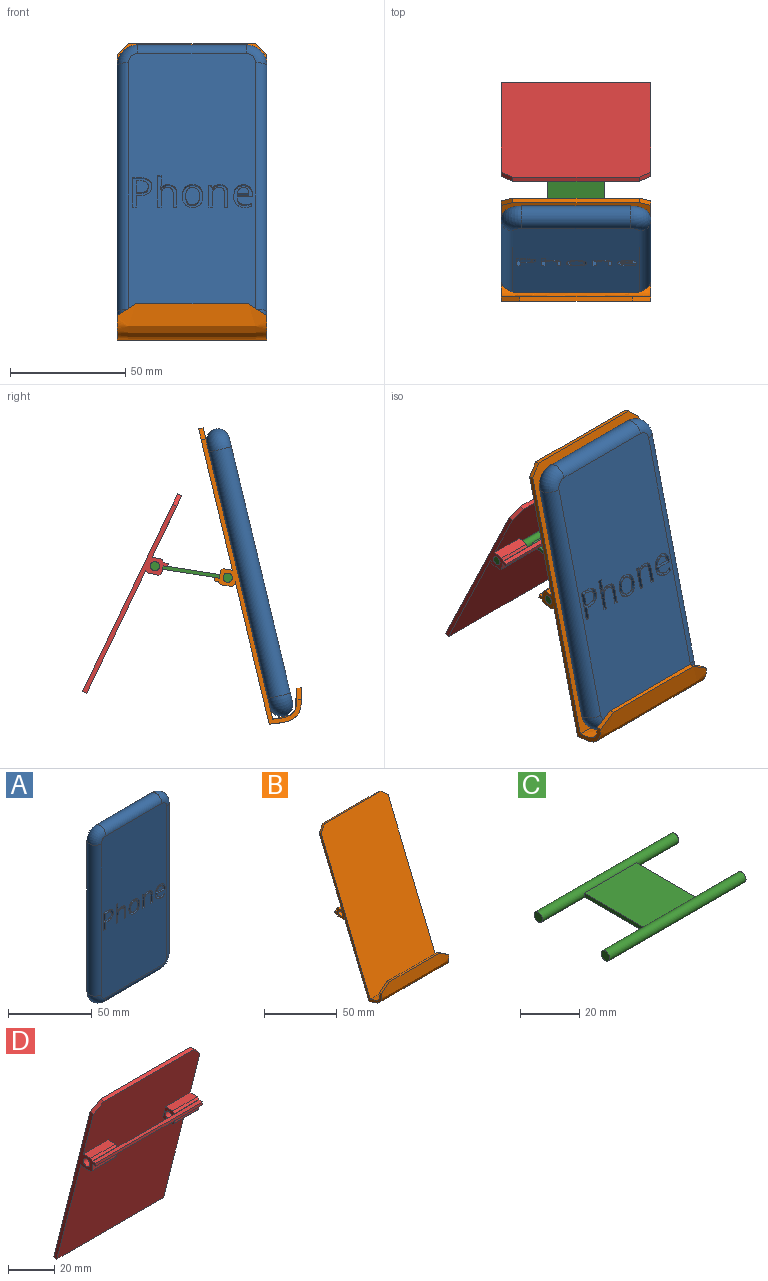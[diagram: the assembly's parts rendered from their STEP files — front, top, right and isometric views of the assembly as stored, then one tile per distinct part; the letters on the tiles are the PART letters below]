
ASSEMBLY  parts=4 mates=3
PART A: 104 faces, bbox 65x10x128 mm
  f0: plane 118x55mm, normal (0,-1,0), area 6209.6mm2, adj f2,f3,f4,f5,f6,f7,f8,f9
  f1: plane 118x55mm, normal (0,1,0), area 6476.3mm2, adj f2,f3,f4,f5,f6,f7,f8,f9
  f2: cylinder r=5mm len=110mm, axis (0,0,1), area 1727.9mm2, adj f0,f1,f3,f4
  f3: torus R=4mm, axis (0,-1,0), area 177.2mm2, adj f0,f1,f2,f5
  f4: torus R=4mm, axis (0,-1,0), area 177.2mm2, adj f0,f1,f2,f6
  f5: cylinder r=5mm len=47mm, axis (-1,0,0), area 738.3mm2, adj f0,f1,f3,f7
  f6: cylinder r=5mm len=47mm, axis (1,0,0), area 738.3mm2, adj f0,f1,f4,f8
  f7: torus R=4mm, axis (0,-1,0), area 177.2mm2, adj f0,f1,f5,f9
  f8: torus R=4mm, axis (0,-1,0), area 177.2mm2, adj f0,f1,f6,f9
  f9: cylinder r=5mm len=110mm, axis (0,0,-1), area 1727.9mm2, adj f0,f1,f7,f8
  f10: plane 6.33x2mm, normal (1,0,0), area 12.7mm2, adj f0,f11,f27,f28
  f11: plane 2x1.48mm, normal (0,0,1), area 3mm2, adj f0,f10,f12,f28
  f12: plane 6.38x2mm, normal (-1,0,0), area 12.8mm2, adj f0,f11,f13,f28
  f13: extruded ~2.71x2mm, area 5.9mm2, adj f0,f12,f14,f28
  f14: extruded ~2.69x2mm, area 5.8mm2, adj f0,f13,f15,f28
  f15: extruded ~2x1.84mm, area 3.8mm2, adj f0,f14,f16,f28
  f16: extruded ~2x1.25mm, area 3.4mm2, adj f0,f15,f17,f28
  f17: plane 2x0.09mm, normal (0,0,-1), area 0.2mm2, adj f0,f16,f18,f28
  f18: extruded ~2x1.26mm, area 2.5mm2, adj f0,f17,f19,f28
  f19: plane 4.21x2mm, normal (-1,0,0), area 8.4mm2, adj f0,f18,f20,f28
  f20: plane 2x1.48mm, normal (0,0,-1), area 3mm2, adj f0,f19,f21,f28
  f21: plane 13.9x2mm, normal (1,0,0), area 27.8mm2, adj f0,f20,f22,f28
  f22: plane 2x1.48mm, normal (0,0,1), area 3mm2, adj f0,f21,f23,f28
  f23: plane 5.12x2mm, normal (-1,0,0), area 10.2mm2, adj f0,f22,f24,f28
  f24: extruded ~2.75x2mm, area 5.8mm2, adj f0,f23,f25,f28
  f25: extruded ~2.25x2mm, area 5mm2, adj f0,f24,f26,f28
  f26: extruded ~2x1.71mm, area 3.7mm2, adj f0,f25,f27,f28
  f27: extruded ~2x1.78mm, area 3.8mm2, adj f0,f10,f26,f28
  f28: plane 13.9x8.18mm, normal (0,-1,0), area 40.9mm2, adj f10,f11,f12,f13,f14,f15,f16,f17
  f29: extruded ~2x1.88mm, area 4.2mm2, adj f30,f47,f48,f101
  f30: extruded ~2x1.79mm, area 4mm2, adj f29,f31,f48,f101
  f31: extruded ~2.15x2mm, area 4.6mm2, adj f30,f32,f48,f101
  f32: plane 5.12x2mm, normal (0,0,-1), area 10.2mm2, adj f31,f47,f48,f101
  f33: extruded ~3.43x2mm, area 7.6mm2, adj f0,f34,f46,f48
  f34: extruded ~2x1.69mm, area 3.4mm2, adj f0,f33,f35,f48
  f35: extruded ~2x1.49mm, area 3.1mm2, adj f0,f34,f36,f48
  f36: plane 2x1.32mm, normal (-1,0,0), area 2.6mm2, adj f0,f35,f37,f48
  f37: extruded ~3.12x2mm, area 6.4mm2, adj f0,f36,f38,f48
  f38: extruded ~2.33x2mm, area 5.1mm2, adj f0,f37,f39,f48
  f39: extruded ~2.62x2mm, area 5.6mm2, adj f0,f38,f40,f48
  f40: plane 6.74x2mm, normal (0,0,1), area 13.5mm2, adj f0,f39,f41,f48
  f41: plane 2x0.94mm, normal (-1,0,0), area 1.9mm2, adj f0,f40,f42,f48
  f42: extruded ~3.19x2mm, area 6.9mm2, adj f0,f41,f43,f48
  f43: extruded ~2.91x2mm, area 6.5mm2, adj f0,f42,f44,f48
  f44: extruded ~3.13x2mm, area 7.1mm2, adj f0,f43,f45,f48
  f45: extruded ~3.76x2mm, area 8mm2, adj f0,f44,f46,f48
  f46: extruded ~3.67x2mm, area 8mm2, adj f0,f33,f45,f48
  f47: extruded ~2.12x2mm, area 4.6mm2, adj f29,f32,f48,f101
  f48: plane 10.15x8.28mm, normal (0,-1,0), area 38.2mm2, adj f29,f30,f31,f32,f33,f34,f35,f36
  f49: extruded ~2.86x2mm, area 6mm2, adj f50,f65,f66,f102
  f50: extruded ~2.85x2mm, area 6mm2, adj f49,f51,f66,f102
  f51: extruded ~2.2x2mm, area 5mm2, adj f50,f52,f66,f102
  f52: extruded ~2.23x2mm, area 5mm2, adj f51,f53,f66,f102
  f53: extruded ~2.84x2mm, area 6mm2, adj f52,f54,f66,f102
  f54: extruded ~2.86x2mm, area 6mm2, adj f53,f55,f66,f102
  f55: extruded ~2.21x2mm, area 5mm2, adj f54,f65,f66,f102
  f56: extruded ~3.74x2mm, area 8mm2, adj f0,f57,f64,f66
  f57: extruded ~3.7x2mm, area 8mm2, adj f0,f56,f58,f66
  f58: extruded ~3.26x2mm, area 7.3mm2, adj f0,f57,f59,f66
  f59: extruded ~3.32x2mm, area 7.4mm2, adj f0,f58,f60,f66
  f60: extruded ~3.73x2mm, area 8mm2, adj f0,f59,f61,f66
  f61: extruded ~2.7x2mm, area 5.6mm2, adj f0,f60,f62,f66
  f62: extruded ~2x1.77mm, area 4.8mm2, adj f0,f61,f63,f66
  f63: extruded ~2.33x2mm, area 4.9mm2, adj f0,f62,f64,f66
  f64: extruded ~3.33x2mm, area 7.4mm2, adj f0,f56,f63,f66
  f65: extruded ~2.2x2mm, area 5mm2, adj f49,f55,f66,f102
  f66: plane 10.15x8.99mm, normal (0,-1,0), area 36.8mm2, adj f49,f50,f51,f52,f53,f54,f55,f56
  f67: plane 2x1.37mm, normal (0,0,-1), area 2.7mm2, adj f68,f81,f82,f103
  f68: plane 5.3x2mm, normal (-1,0,0), area 10.6mm2, adj f67,f69,f82,f103
  f69: plane 2x1.7mm, normal (0,0,1), area 3.4mm2, adj f68,f70,f82,f103
  f70: extruded ~2.64x2mm, area 5.5mm2, adj f69,f71,f82,f103
  f71: extruded ~2x1.93mm, area 4.4mm2, adj f70,f72,f82,f103
  f72: extruded ~2.09x2mm, area 4.7mm2, adj f71,f81,f82,f103
  f73: extruded ~3.05x2mm, area 6.9mm2, adj f0,f74,f80,f82
  f74: extruded ~4.89x3.8mm, area 14.2mm2, adj f0,f73,f75,f82
  f75: plane 3.39x2mm, normal (0,0,-1), area 6.8mm2, adj f0,f74,f76,f82
  f76: plane 13.06x2mm, normal (1,0,0), area 26.1mm2, adj f0,f75,f77,f82
  f77: plane 2x1.52mm, normal (0,0,1), area 3mm2, adj f0,f76,f78,f82
  f78: plane 5.14x2mm, normal (-1,0,0), area 10.3mm2, adj f0,f77,f79,f82
  f79: plane 2x1.54mm, normal (0,0,1), area 3.1mm2, adj f0,f78,f80,f82
  f80: extruded ~3.87x2mm, area 8.2mm2, adj f0,f73,f79,f82
  f81: extruded ~2.92x2mm, area 6.1mm2, adj f67,f72,f82,f103
  f82: plane 13.06x8.28mm, normal (0,-1,0), area 42mm2, adj f67,f68,f69,f70,f71,f72,f73,f74
  f83: plane 6.33x2mm, normal (1,0,0), area 12.7mm2, adj f0,f84,f99,f100
  f84: plane 2x1.48mm, normal (0,0,1), area 3mm2, adj f0,f83,f85,f100
  f85: plane 6.38x2mm, normal (-1,0,0), area 12.8mm2, adj f0,f84,f86,f100
  f86: extruded ~2.73x2mm, area 5.9mm2, adj f0,f85,f87,f100
  f87: extruded ~2.66x2mm, area 5.7mm2, adj f0,f86,f88,f100
  f88: extruded ~2x1.83mm, area 3.8mm2, adj f0,f87,f89,f100
  f89: extruded ~2x1.28mm, area 3.4mm2, adj f0,f88,f90,f100
  f90: plane 2x0.07mm, normal (0,0,-1), area 0.1mm2, adj f0,f89,f91,f100
  f91: plane 2x1.34mm, normal (-0.98,0,-0.18), area 2.7mm2, adj f0,f90,f92,f100
  f92: plane 2x1.21mm, normal (0,0,-1), area 2.4mm2, adj f0,f91,f93,f100
  f93: plane 9.79x2mm, normal (1,0,0), area 19.6mm2, adj f0,f92,f94,f100
  f94: plane 2x1.48mm, normal (0,0,1), area 3mm2, adj f0,f93,f95,f100
  f95: plane 5.14x2mm, normal (-1,0,0), area 10.3mm2, adj f0,f94,f96,f100
  f96: extruded ~2.74x2mm, area 5.8mm2, adj f0,f95,f97,f100
  f97: extruded ~2.25x2mm, area 5mm2, adj f0,f96,f98,f100
  f98: extruded ~2x1.71mm, area 3.7mm2, adj f0,f97,f99,f100
  f99: extruded ~2x1.78mm, area 3.8mm2, adj f0,f83,f98,f100
  f100: plane 9.97x8.18mm, normal (0,-1,0), area 34.7mm2, adj f83,f84,f85,f86,f87,f88,f89,f90
  f101: plane 5.12x2.89mm, normal (0,-1,0), area 11.9mm2, adj f29,f30,f31,f32,f47
  f102: plane 7.64x5.92mm, normal (0,-1,0), area 37.6mm2, adj f49,f50,f51,f52,f53,f54,f55,f65
  f103: plane 5.3x5.19mm, normal (0,-1,0), area 24.5mm2, adj f67,f68,f69,f70,f71,f72,f81
PART B: 36 faces, bbox 65x62.6x122.6 mm
  f0: plane 15x3.3mm, normal (0,1,0), area 49.5mm2, adj f6,f15,f27,f33
  f1: plane 15x0.2mm, normal (0,1,0), area 3mm2, adj f4,f21,f24,f34
  f2: plane 121.78x65mm, normal (0,0.92,-0.38), area 8383.6mm2, adj f3,f4,f6,f9,f10,f14,f15,f16
  f3: plane 55x1.85mm, normal (0,0.38,0.92), area 110mm2, adj f2,f8,f28,f29
  f4: plane 117.92x60.71mm, normal (-1,0,0), area 320.8mm2, adj f1,f2,f7,f8,f9,f16,f17,f18
  f5: plane 49x1.96mm, normal (0,0.21,0.98), area 98mm2, adj f7,f9,f30,f31
  f6: plane 117.92x60.71mm, normal (1,0,0), area 320.8mm2, adj f0,f2,f7,f8,f9,f10,f11,f12
  f7: extruded ~65x14.92mm, area 1294.1mm2, adj f4,f5,f6,f8,f30,f31
  f8: plane 120.17x65mm, normal (0,-0.92,0.38), area 8425mm2, adj f3,f4,f6,f7,f28,f29
  f9: extruded ~65x17.71mm, area 1605.3mm2, adj f2,f4,f5,f6,f30,f31
  f10: plane 15x1.22mm, normal (0,-1,0), area 18.3mm2, adj f2,f6,f15,f23
  f11: plane 15x5mm, normal (0,0,-1), area 75mm2, adj f6,f15,f23,f26
  f12: plane 15x0.2mm, normal (0,1,0), area 3mm2, adj f6,f15,f26,f34
  f13: cylinder r=2mm len=15mm, axis (1,0,0), area 188.5mm2, adj f6,f15
  f14: plane 15x4.03mm, normal (0,0,1), area 60.4mm2, adj f2,f6,f15,f27
  f15: plane 7x7mm, normal (-1,0,0), area 30.2mm2, adj f0,f2,f10,f11,f12,f13,f14,f23
  f16: plane 15x4.03mm, normal (0,0,1), area 60.4mm2, adj f2,f4,f21,f25
  f17: plane 15x3.3mm, normal (0,1,0), area 49.5mm2, adj f4,f21,f25,f33
  f18: plane 15x5mm, normal (0,0,-1), area 75mm2, adj f4,f21,f22,f24
  f19: cylinder r=2mm len=15mm, axis (-1,0,0), area 188.5mm2, adj f4,f21
  f20: plane 15x1.22mm, normal (0,-1,0), area 18.3mm2, adj f2,f4,f21,f22
  f21: plane 7x7mm, normal (1,0,0), area 30.2mm2, adj f1,f2,f16,f17,f18,f19,f20,f22
  f22: plane 15x1mm, normal (0,-0.71,-0.71), area 21.2mm2, adj f4,f18,f20,f21
  f23: plane 15x1mm, normal (0,-0.71,-0.71), area 21.2mm2, adj f6,f10,f11,f15
  f24: plane 15x1mm, normal (0,0.71,-0.71), area 21.2mm2, adj f1,f4,f18,f21
  f25: plane 15x1mm, normal (0,0.71,0.71), area 21.2mm2, adj f4,f16,f17,f21
  f26: plane 15x1mm, normal (0,0.71,-0.71), area 21.2mm2, adj f6,f11,f12,f15
  f27: plane 15x1mm, normal (0,0.71,0.71), area 21.2mm2, adj f0,f6,f14,f15
  f28: plane 5.39x5mm, normal (-0.71,0.27,0.65), area 14.1mm2, adj f2,f3,f4,f8
  f29: plane 5.39x5mm, normal (0.71,0.27,0.65), area 14.1mm2, adj f2,f3,f6,f8
  f30: plane 8.02x5.35mm, normal (-0.53,0.17,0.83), area 18.9mm2, adj f4,f5,f7,f9
  f31: plane 8.02x5.35mm, normal (0.53,0.17,0.83), area 18.9mm2, adj f5,f6,f7,f9
  f32: plane 35x1.5mm, normal (0,-1,0), area 52.5mm2, adj f15,f21,f33,f34
  f33: plane 65x2mm, normal (0,0,1), area 130mm2, adj f0,f4,f6,f17,f32,f35
  f34: plane 65x2mm, normal (0,0,-1), area 130mm2, adj f1,f4,f6,f12,f32,f35
  f35: plane 65x1.5mm, normal (0,1,0), area 97.5mm2, adj f4,f6,f33,f34
PART C: 10 faces, bbox 65x36x4 mm
  f0: plane 28.33x1.6mm, normal (1,0,0), area 45mm2, adj f1,f3,f4,f7
  f1: plane 28.33x25mm, normal (0,0,-1), area 708.3mm2, adj f0,f2,f4,f7
  f2: plane 28.33x1.6mm, normal (-1,0,0), area 45mm2, adj f1,f3,f4,f7
  f3: plane 28.33x25mm, normal (0,0,1), area 708.3mm2, adj f0,f2,f4,f7
  f4: cylinder r=2mm len=65mm, axis (1,0,0), area 775.7mm2, adj f0,f1,f2,f3,f5,f6
  f5: plane 4x4mm, normal (1,0,0), area 12.6mm2, adj f4
  f6: plane 4x4mm, normal (-1,0,0), area 12.6mm2, adj f4
  f7: cylinder r=2mm len=65mm, axis (1,0,0), area 775.7mm2, adj f0,f1,f2,f3,f8,f9
  f8: plane 4x4mm, normal (1,0,0), area 12.6mm2, adj f7
  f9: plane 4x4mm, normal (-1,0,0), area 12.6mm2, adj f7
PART D: 30 faces, bbox 65x25.5x92.7 mm
  f0: plane 15x0.2mm, normal (0,-1,0), area 3mm2, adj f3,f8,f10,f27
  f1: plane 15x0.2mm, normal (0,-1,0), area 3mm2, adj f12,f17,f23,f27
  f2: plane 15x4.45mm, normal (0,0,1), area 66.7mm2, adj f3,f8,f10,f11
  f3: plane 7x6.98mm, normal (-1,0,0), area 30.2mm2, adj f0,f2,f4,f5,f6,f7,f9,f10
  f4: plane 15x0.98mm, normal (0,0.71,-0.71), area 20.8mm2, adj f3,f6,f8,f11
  f5: plane 15x3.3mm, normal (0,-1,0), area 49.5mm2, adj f3,f8,f9,f29
  f6: plane 15x5mm, normal (0,0,-1), area 75mm2, adj f3,f4,f8,f9
  f7: cylinder r=2mm len=15mm, axis (1,0,0), area 188.5mm2, adj f3,f8
  f8: plane 87.89x25.52mm, normal (1,0,0), area 213.6mm2, adj f0,f2,f4,f5,f6,f7,f9,f10
  f9: plane 15x1mm, normal (0,-0.71,-0.71), area 21.2mm2, adj f3,f5,f6,f8
  f10: plane 15x1mm, normal (0,-0.71,0.71), area 21.2mm2, adj f0,f2,f3,f8
  f11: plane 92.25x65mm, normal (0,-0.97,-0.25), area 5975.2mm2, adj f2,f3,f4,f8,f12,f13,f14,f16
  f12: plane 87.89x25.52mm, normal (-1,0,0), area 213.6mm2, adj f1,f11,f14,f15,f16,f18,f19,f20
  f13: plane 55x1.94mm, normal (0,-0.25,0.97), area 110mm2, adj f11,f15,f24,f25
  f14: plane 65x1.94mm, normal (0,0.25,-0.97), area 130mm2, adj f8,f11,f12,f15
  f15: plane 92.25x65mm, normal (0,0.97,0.25), area 6161.6mm2, adj f8,f12,f13,f14,f24,f25
  f16: plane 15x4.45mm, normal (0,0,1), area 66.7mm2, adj f11,f12,f17,f23
  f17: plane 7x6.98mm, normal (1,0,0), area 30.2mm2, adj f1,f11,f16,f18,f19,f20,f21,f22
  f18: plane 15x0.98mm, normal (0,0.71,-0.71), area 20.8mm2, adj f11,f12,f17,f20
  f19: plane 15x3.3mm, normal (0,-1,0), area 49.5mm2, adj f12,f17,f22,f29
  f20: plane 15x5mm, normal (0,0,-1), area 75mm2, adj f12,f17,f18,f22
  f21: cylinder r=2mm len=15mm, axis (-1,0,0), area 188.5mm2, adj f12,f17
  f22: plane 15x1mm, normal (0,-0.71,-0.71), area 21.2mm2, adj f12,f17,f19,f20
  f23: plane 15x1mm, normal (0,-0.71,0.71), area 21.2mm2, adj f1,f12,f16,f17
  f24: plane 5.34x5mm, normal (0.71,-0.17,0.69), area 14.1mm2, adj f8,f11,f13,f15
  f25: plane 5.34x5mm, normal (-0.71,-0.17,0.69), area 14.1mm2, adj f11,f12,f13,f15
  f26: plane 35x1.5mm, normal (0,1,0), area 52.5mm2, adj f3,f17,f27,f29
  f27: plane 65x2mm, normal (0,0,1), area 130mm2, adj f0,f1,f8,f12,f26,f28
  f28: plane 65x1.5mm, normal (0,-1,0), area 97.5mm2, adj f8,f12,f27,f29
  f29: plane 65x2mm, normal (0,0,-1), area 130mm2, adj f5,f8,f12,f19,f26,f28
PLACE A rot(axis=(-1,0,0),13.5deg) t=(10.92,-67.6,3.73)mm
PLACE B rot(axis=(1,0,0),9deg) t=(-24.81,-66.08,9.3)mm
PLACE C rot(axis=(1,0,0),9deg) t=(-24.81,-66.08,9.3)mm
PLACE D rot(axis=(1,0,0),11.4deg) t=(-24.81,-65.96,7.77)mm
MATE revolute C.f7 <-> D.f7  axis (1,0,0) through (7.69,-30.47,11.37)mm
MATE revolute C.f4 <-> B.f13  axis (1,0,0) through (7.69,-62.08,6.38)mm
MATE planar B.f8 <-> A.f1  axis (0,-0.97,0.23) through (-24.81,-66.58,8)mm
